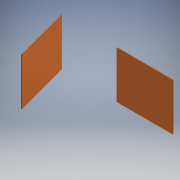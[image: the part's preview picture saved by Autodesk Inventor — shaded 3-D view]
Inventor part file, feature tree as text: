
AUTODESK INVENTOR PART (.ipt)
format: ipt  version: 2016 (Build 200138000, 138)  size: 167,936 bytes
history: native  units: mm
features: extrude x3, sketch x3, projected_geometry x1
ambient origin geometry x8: Origin, YZ Plane, XZ Plane, XY Plane, X Axis, Y Axis, Z Axis, Center Point
bodies: Solid1 (feature_tree)
feature tree (7):
  extrude  "Extrusion1"  Depth=50.0mm
  extrude  "Extrusión10"  Depth=6.0mm
  extrude  "Extrusión11"  TaperAngle=0.0deg  [1 undecoded]
  sketch  "Sketch1"  dims[d2=41.0mm d3=50.0mm]
  sketch  "Boceto10"  dims[d4=100.0mm d5=6.0mm]
  sketch  "Boceto11"  dims[d6=6.0mm d8=0.0mm d49=996.666667mm d50=996.666667mm d52=10.0mm d53=996.666667mm d54=820.0mm d55=0.0mm d56=41.0mm d57=50.0mm d58=100.0mm d59=6.0mm d60=6.0mm d61=820.0mm d62=0.0mm]
  projected_geometry  "Contorno proyectado8"
note: 1 required parameter value undecoded (feature->parameter linkage not recoverable at this tier; creation-order binding heuristic only, values carry confidence <= 0.55)
